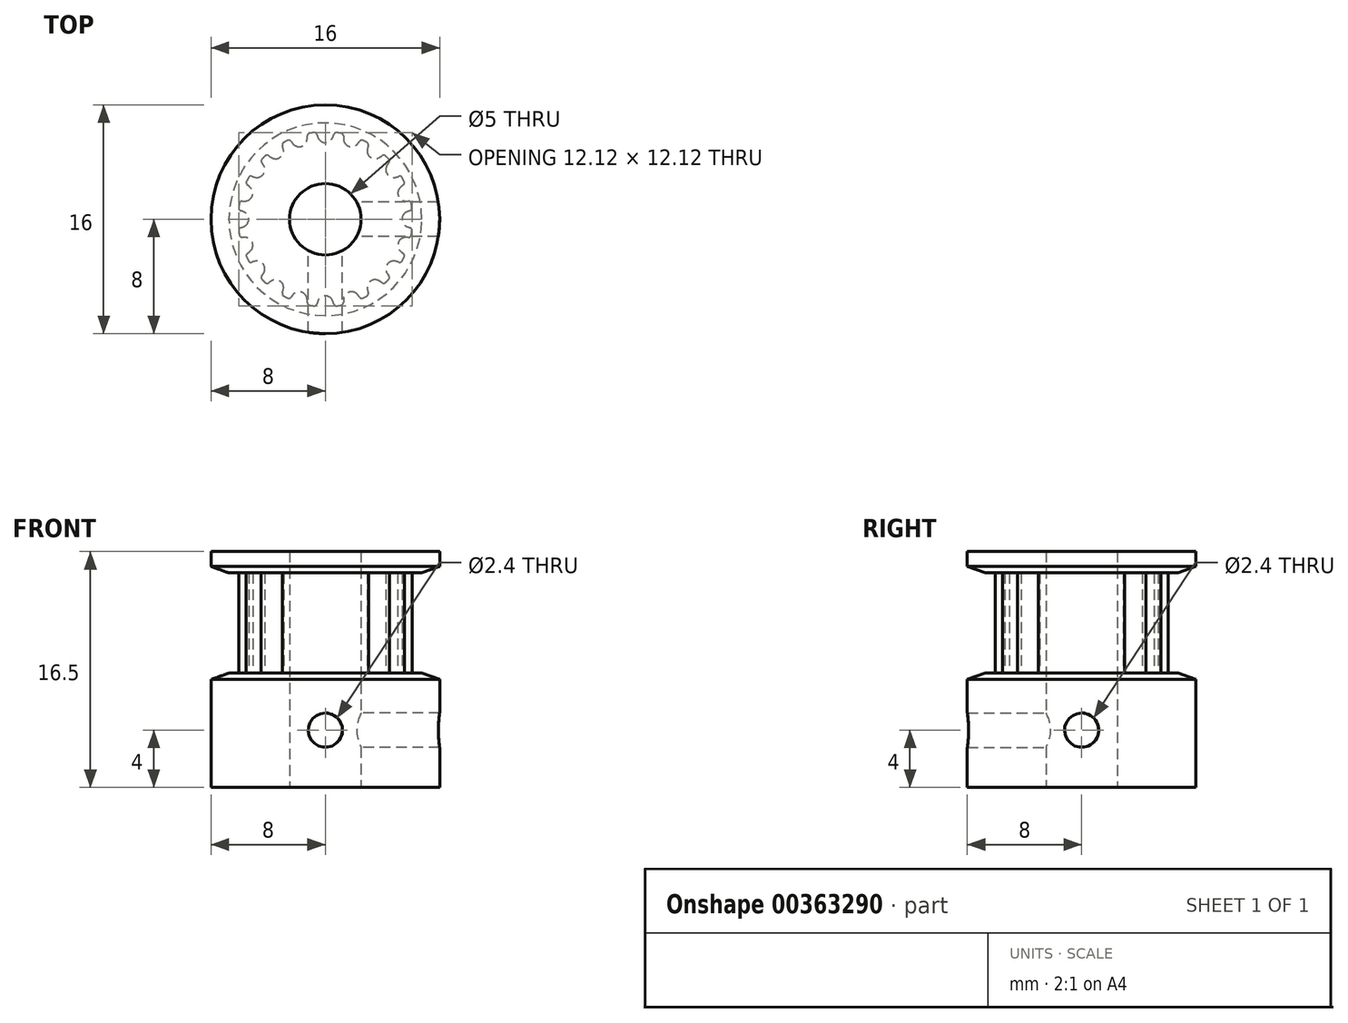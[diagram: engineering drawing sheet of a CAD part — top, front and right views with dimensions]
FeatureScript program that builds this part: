
annotation { "Feature Type Name" : "Feature", "Feature Type Description" : "" }
export const myFeature = defineFeature(function(context is Context, id is Id, definition is map)
    precondition{}
    {
        {
            assignVariable(context, id + "F0", {"name" : "teeth", "anyValue" : 20});
        }
        {
            assignVariable(context, id + "F1", {"name" : "belt_width", "anyValue" : 6 * mm});
        }
        {
            assignVariable(context, id + "F2", {"name" : "bore_diameter", "anyValue" : 5 * mm});
        }
        {
            var Q0;
            Q0=qCreatedBy(makeId("Top.planeOp"),FACE);
            var sketch = newSketch(context, id + "F3", { "sketchPlane" : qUnion([Q0])});
            skLineSegment(sketch, "E0", {"start": v(0, 0) * mm, "end": v(0, 5.36) * mm, "construction": true});
            skCircle(sketch, "E1", {"center": v(0, 0) * mm, "radius": 6.11 * mm});
            skPoint(sketch, "E2.MirrorCS.end.orphan", {"position": v(0.96, 6.04) * mm});
            skLineSegment(sketch, "E3", {"start": v(0.96, 6.04) * mm, "end": v(1, 6.29) * mm, "construction": true});
            skLineSegment(sketch, "E4", {"start": v(-0.96, 6.04) * mm, "end": v(-1, 6.29) * mm, "construction": true});
            skArc(sketch, "E5", {"start": v(0, 5.36) * mm, "mid": v(0.31, 5.46) * mm, "end": v(0.52, 5.72) * mm});
            skArc(sketch, "E6", {"start": v(0.52, 5.72) * mm, "mid": v(0.56, 5.83) * mm, "end": v(0.58, 5.94) * mm, "construction": true});
            skLineSegment(sketch, "E7", {"start": v(0, 5.36) * mm, "end": v(0, 6.11) * mm, "construction": true});
            skLineSegment(sketch, "E8", {"start": v(0, 6.11) * mm, "end": v(0, 6.37) * mm, "construction": true});
            skArc(sketch, "E9", {"start": v(0.58, 5.94) * mm, "mid": v(0.64, 6.04) * mm, "end": v(0.75, 6.07) * mm, "construction": true});
            skArc(sketch, "E10", {"start": v(1, 6.29) * mm, "mid": v(0, 6.37) * mm, "end": v(-1, 6.29) * mm, "construction": true});
            skLineSegment(sketch, "E11", {"start": v(0.96, 6.04) * mm, "end": v(0.84, 5.3) * mm});
            skLineSegment(sketch, "E12", {"start": v(0.84, 5.3) * mm, "end": v(0, 0) * mm});
            skLineSegment(sketch, "E13", {"start": v(0, 0) * mm, "end": v(-0.84, 5.3) * mm});
            skLineSegment(sketch, "E14", {"start": v(-0.84, 5.3) * mm, "end": v(-0.96, 6.04) * mm});
            skArc(sketch, "E15", {"start": v(0.8, 6.06) * mm, "mid": v(0.67, 6.03) * mm, "end": v(0.6, 5.93) * mm});
            skArc(sketch, "E16", {"start": v(0.52, 5.72) * mm, "mid": v(0.56, 5.83) * mm, "end": v(0.6, 5.93) * mm});
            skArc(sketch, "E17.MirrorCS", {"start": v(0, 5.36) * mm, "mid": v(-0.31, 5.46) * mm, "end": v(-0.52, 5.72) * mm});
            skArc(sketch, "E18.MirrorCS", {"start": v(-0.52, 5.72) * mm, "mid": v(-0.56, 5.83) * mm, "end": v(-0.6, 5.93) * mm});
            skArc(sketch, "E19.MirrorCS", {"start": v(-0.8, 6.06) * mm, "mid": v(-0.67, 6.03) * mm, "end": v(-0.6, 5.93) * mm});
            skArc(sketch, "E20", {"start": v(0, 6.11) * mm, "mid": v(-0.2, 6.1) * mm, "end": v(-0.4, 6.1) * mm});
            skArc(sketch, "E21", {"start": v(0.84, 5.3) * mm, "mid": v(0, 5.36) * mm, "end": v(-0.84, 5.3) * mm, "construction": true});
            skLineSegment(sketch, "E22", {"start": v(1, 6.29) * mm, "end": v(1.05, 6.66) * mm, "construction": true});
            skLineSegment(sketch, "E23", {"start": v(-1, 6.29) * mm, "end": v(-1.05, 6.66) * mm, "construction": true});
            skArc(sketch, "E24", {"start": v(-1.05, 6.66) * mm, "mid": v(0, 6.74) * mm, "end": v(1.05, 6.66) * mm, "construction": true});
            skSolve(sketch);
        }
        {
            var Q0;
            Q0=makeQuery(id+"F3.imprint","IMPRINT",FACE,{"disambiguationData":[TD([[makeQuery(id+"F3.imprint","IMPRINT",EDGE,{"derivedFrom":sQuery(id+"F3.wireOp",EDGE,"E5")}),-1.0]])]});
            var Q1;
            {var subQ1=sQuery(id+"F3.wireOp",EDGE,"E14");Q1=makeQuery(id+"F3.imprint","IMPRINT",FACE,{"disambiguationData":[TD([[makeQuery(id+"F3.imprint","IMPRINT",EDGE,{"derivedFrom":subQ1}),-1.0]])]});}
            var Q2;
            {var subQ0=sQuery(id+"F3.wireOp",EDGE,"E12");Q2=makeQuery(id+"F3.imprint","IMPRINT",FACE,{"disambiguationData":[TD([[makeQuery(id+"F3.imprint","IMPRINT",EDGE,{"derivedFrom":subQ0}),-1.0]])]});}
            extrude(context, id + "F4", {"entities" : qUnion([Q0, Q1, Q2]), "endBound" : BoundingType.SYMMETRIC, "depth" : (getVariable(context, 'belt_width')) + 1 * mm});
        }
        {
            var Q0;
            Q0=makeQuery(id+"F4.opExtrude","SWEPT_BODY",BODY,{"disambiguationData":[OSD([sQuery(id+"F3.wireOp",EDGE,"E1"),sQuery(id+"F3.wireOp",EDGE,"E5"),sQuery(id+"F3.wireOp",EDGE,"E11"),sQuery(id+"F3.wireOp",EDGE,"E12"),sQuery(id+"F3.wireOp",EDGE,"E13"),sQuery(id+"F3.wireOp",EDGE,"E14"),sQuery(id+"F3.wireOp",EDGE,"E15"),sQuery(id+"F3.wireOp",EDGE,"E16"),sQuery(id+"F3.wireOp",EDGE,"E17.MirrorCS"),sQuery(id+"F3.wireOp",EDGE,"E18.MirrorCS"),sQuery(id+"F3.wireOp",EDGE,"E19.MirrorCS")])]});
            var Q1;
            Q1=makeQuery(id+"F4.opExtrude","SWEPT_EDGE",EDGE,{"disambiguationData":[OSD([sQuery(id+"F3.wireOp",EDGE,"E12"),sQuery(id+"F3.wireOp",EDGE,"E13")])]});
            circularPattern(context, id + "F5", {"operationType" : NewBodyOperationType.ADD, "entities" : qUnion([Q0]), "axis" : qUnion([Q1]), "angle" : 360 * degree, "instanceCount" : getVariable(context, 'teeth'), "equalSpace" : true});
        }
        {
            var Q0;
            Q0=qCreatedBy(makeId("Front.planeOp"),FACE);
            var sketch = newSketch(context, id + "F6", { "sketchPlane" : qUnion([Q0])});
            skLineSegment(sketch, "E25", {"start": v(0, -3.5) * mm, "end": v(6.74, -3.5) * mm});
            skLineSegment(sketch, "E26", {"start": v(6.74, -3.5) * mm, "end": v(8, -3.96) * mm});
            skLineSegment(sketch, "E27", {"start": v(8, -3.96) * mm, "end": v(8, -11.5) * mm});
            skLineSegment(sketch, "E28", {"start": v(8, -11.5) * mm, "end": v(0, -11.5) * mm});
            skLineSegment(sketch, "E29", {"start": v(0, -11.5) * mm, "end": v(0, -3.5) * mm});
            skLineSegment(sketch, "E30", {"start": v(0, 3.5) * mm, "end": v(6.74, 3.5) * mm});
            skLineSegment(sketch, "E31", {"start": v(8, 3.96) * mm, "end": v(6.74, 3.5) * mm});
            skLineSegment(sketch, "E32", {"start": v(8, 3.96) * mm, "end": v(8, 5) * mm});
            skLineSegment(sketch, "E33", {"start": v(8, 5) * mm, "end": v(0, 5) * mm});
            skLineSegment(sketch, "E34", {"start": v(0, 5) * mm, "end": v(0, 3.5) * mm});
            skLineSegment(sketch, "E35", {"start": v(6.74, -3.5) * mm, "end": v(8, -3.5) * mm, "construction": true});
            skLineSegment(sketch, "E36", {"start": v(8, -3.5) * mm, "end": v(8, -3.96) * mm, "construction": true});
            skLineSegment(sketch, "E37", {"start": v(6.74, 3.5) * mm, "end": v(8, 3.5) * mm, "construction": true});
            skLineSegment(sketch, "E38", {"start": v(8, 3.5) * mm, "end": v(8, 3.96) * mm, "construction": true});
            skLineSegment(sketch, "E39", {"start": v(6.11, 0) * mm, "end": v(6.11, -3.5) * mm, "construction": true});
            skSolve(sketch);
        }
        {
            var Q0;
            Q0=qSketchRegion(id+"F6",true);
            var Q1;
            Q1=qConstructionFilter(qBodyType(qCreatedBy(id+"F6",EDGE),BodyType.WIRE),ConstructionObject.NO);
            var Q2;
            Q2=sQuery(id+"F6.wireOp",EDGE,"E29");
            revolve(context, id + "F7", {"operationType" : NewBodyOperationType.ADD, "entities" : qUnion([Q0]), "surfaceEntities" : qUnion([Q1]), "axis" : qUnion([Q2]), "revolveType" : RevolveType.FULL});
        }
        {
            var Q0;
            Q0=makeQuery(id+"F7.opRevolve","SWEPT_FACE",FACE,{"disambiguationData":[OSD([sQuery(id+"F6.wireOp",EDGE,"E28")])]});
            var sketch = newSketch(context, id + "F8", { "sketchPlane" : qUnion([Q0])});
            skPoint(sketch, "E40", {"position": v(0, 0) * mm});
            skSolve(sketch);
        }
        {
            var Q0;
            Q0=sQuery(id+"F8.wireOp",VERTEX,"E40");
            var Q1;
            Q1=makeQuery(id+"F4.opExtrude","SWEPT_BODY",BODY,{"disambiguationData":[OSD([sQuery(id+"F3.wireOp",EDGE,"E1"),sQuery(id+"F3.wireOp",EDGE,"E5"),sQuery(id+"F3.wireOp",EDGE,"E11"),sQuery(id+"F3.wireOp",EDGE,"E12"),sQuery(id+"F3.wireOp",EDGE,"E13"),sQuery(id+"F3.wireOp",EDGE,"E14"),sQuery(id+"F3.wireOp",EDGE,"E15"),sQuery(id+"F3.wireOp",EDGE,"E16"),sQuery(id+"F3.wireOp",EDGE,"E17.MirrorCS"),sQuery(id+"F3.wireOp",EDGE,"E18.MirrorCS"),sQuery(id+"F3.wireOp",EDGE,"E19.MirrorCS")])]});
            hole(context, id + "F9", {"style" : HoleStyle.SIMPLE, "holeDiameter" : getVariable(context, 'bore_diameter'), "endStyle" : HoleEndStyle.THROUGH, "locations" : qUnion([Q0]), "scope" : qUnion([Q1]), "isTappedThrough" : true});
        }
        {
            var Q0;
            Q0=qCreatedBy(makeId("Front.planeOp"),FACE);
            var sketch = newSketch(context, id + "F10", { "sketchPlane" : qUnion([Q0])});
            skPoint(sketch, "E41", {"position": v(0, -7.5) * mm});
            skLineSegment(sketch, "E42", {"start": v(0, -11.5) * mm, "end": v(0, -3.5) * mm});
            skSolve(sketch);
        }
        {
            var Q0;
            Q0=qCreatedBy(makeId("Right.planeOp"),FACE);
            var sketch = newSketch(context, id + "F11", { "sketchPlane" : qUnion([Q0])});
            skPoint(sketch, "E43", {"position": v(0, -7.5) * mm});
            skSolve(sketch);
        }
        {
            var Q0;
            Q0=sQuery(id+"F10.wireOp",VERTEX,"E41");
            var Q1;
            Q1=makeQuery(id+"F4.opExtrude","SWEPT_BODY",BODY,{"disambiguationData":[OSD([sQuery(id+"F3.wireOp",EDGE,"E1"),sQuery(id+"F3.wireOp",EDGE,"E5"),sQuery(id+"F3.wireOp",EDGE,"E11"),sQuery(id+"F3.wireOp",EDGE,"E12"),sQuery(id+"F3.wireOp",EDGE,"E13"),sQuery(id+"F3.wireOp",EDGE,"E14"),sQuery(id+"F3.wireOp",EDGE,"E15"),sQuery(id+"F3.wireOp",EDGE,"E16"),sQuery(id+"F3.wireOp",EDGE,"E17.MirrorCS"),sQuery(id+"F3.wireOp",EDGE,"E18.MirrorCS"),sQuery(id+"F3.wireOp",EDGE,"E19.MirrorCS")])]});
            hole(context, id + "F12", {"style" : HoleStyle.SIMPLE, "endStyle" : HoleEndStyle.THROUGH, "oppositeDirection" : true, "standardTappedOrClearance" : lookupTablePath({ "standard" : "ISO", "engagement" : "75%", "pitch" : "0.6 mm", "size" : "M3", "type" : "Tapped" }), "standardBlindInLast" : lookupTablePath({ "standard" : "ISO", "engagement" : "75%", "pitch" : "0.6 mm", "size" : "M3", "type" : "Tapped" }), "holeDiameter" : 2.4 * mm, "locations" : qUnion([Q0]), "scope" : qUnion([Q1]), "isTappedThrough" : true, "showTappedDepth" : true});
        }
        {
            var Q0;
            Q0=sQuery(id+"F11.wireOp",VERTEX,"E43");
            var Q1;
            Q1=makeQuery(id+"F4.opExtrude","SWEPT_BODY",BODY,{"disambiguationData":[OSD([sQuery(id+"F3.wireOp",EDGE,"E1"),sQuery(id+"F3.wireOp",EDGE,"E5"),sQuery(id+"F3.wireOp",EDGE,"E11"),sQuery(id+"F3.wireOp",EDGE,"E12"),sQuery(id+"F3.wireOp",EDGE,"E13"),sQuery(id+"F3.wireOp",EDGE,"E14"),sQuery(id+"F3.wireOp",EDGE,"E15"),sQuery(id+"F3.wireOp",EDGE,"E16"),sQuery(id+"F3.wireOp",EDGE,"E17.MirrorCS"),sQuery(id+"F3.wireOp",EDGE,"E18.MirrorCS"),sQuery(id+"F3.wireOp",EDGE,"E19.MirrorCS")])]});
            hole(context, id + "F13", {"style" : HoleStyle.SIMPLE, "endStyle" : HoleEndStyle.THROUGH, "oppositeDirection" : true, "standardTappedOrClearance" : lookupTablePath({ "standard" : "ISO", "engagement" : "75%", "pitch" : "0.6 mm", "size" : "M3", "type" : "Tapped" }), "standardBlindInLast" : lookupTablePath({ "standard" : "ISO", "engagement" : "75%", "pitch" : "0.6 mm", "size" : "M3", "type" : "Tapped" }), "holeDiameter" : 2.4 * mm, "locations" : qUnion([Q0]), "scope" : qUnion([Q1]), "isTappedThrough" : true, "showTappedDepth" : true});
        }
    });
